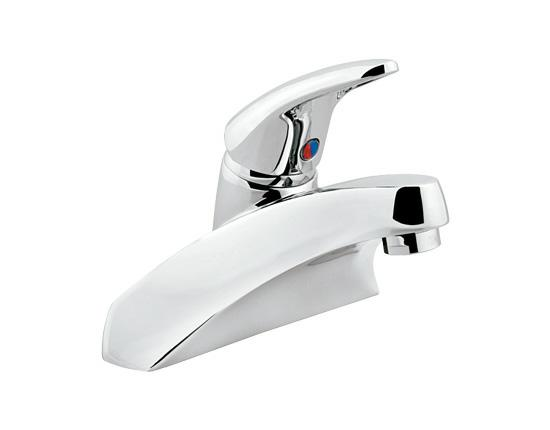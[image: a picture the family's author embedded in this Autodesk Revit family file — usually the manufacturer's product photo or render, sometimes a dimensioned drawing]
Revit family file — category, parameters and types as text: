
# Revit family: Monomando 4 EP92-1.9
name_source: partatom
category: Plumbing Fixtures
revit_build: Autodesk Revit 2015 (Build: 20140223_1515(x64)
units: mm (PartAtom-declared; Revit-internal decimal feet)

## types (1)
- EP92-1.9
    Brass Chromed = Brass
    Default Elevation = 1"
    Description = Mezcladora de 4” con desagüe de push y rebosadero
Mezcladora de 4" con Desagüe de Push
    Features = Monomando de 4" con desagüe de push, con descarga de 1.9 lpm.
instalación de 4" con Valvex V izq. y der. de
discos cerámicos de 1/4 de vuelta.
Mecladora para lavabo con desagüe de push, instalación de 4" con Valvex V izq. y der. de discos cerámicos de 1/4 de vuelta.
    Inlet Threads = ½" - 14 NPSM
    Manufacturer = HELVEX S.A. de C.V.
    Max. Working Pressure = 85.3 psi
    Min. Working Pressure = 2.8 psi
    Model = EP92-1.9
    Satin = Satín Duravex
    Total Height = 5"
    Total Length = 6"
    Total Width = 4"
    Type Comments = Monomando de 4”
    Type Image = EP92-1.9.jpg
    URL = http://www.helvex.com.mx

## geometry (parser evidence)
native form markers: Sweep x3
no freeform markers — native parametric forms only
